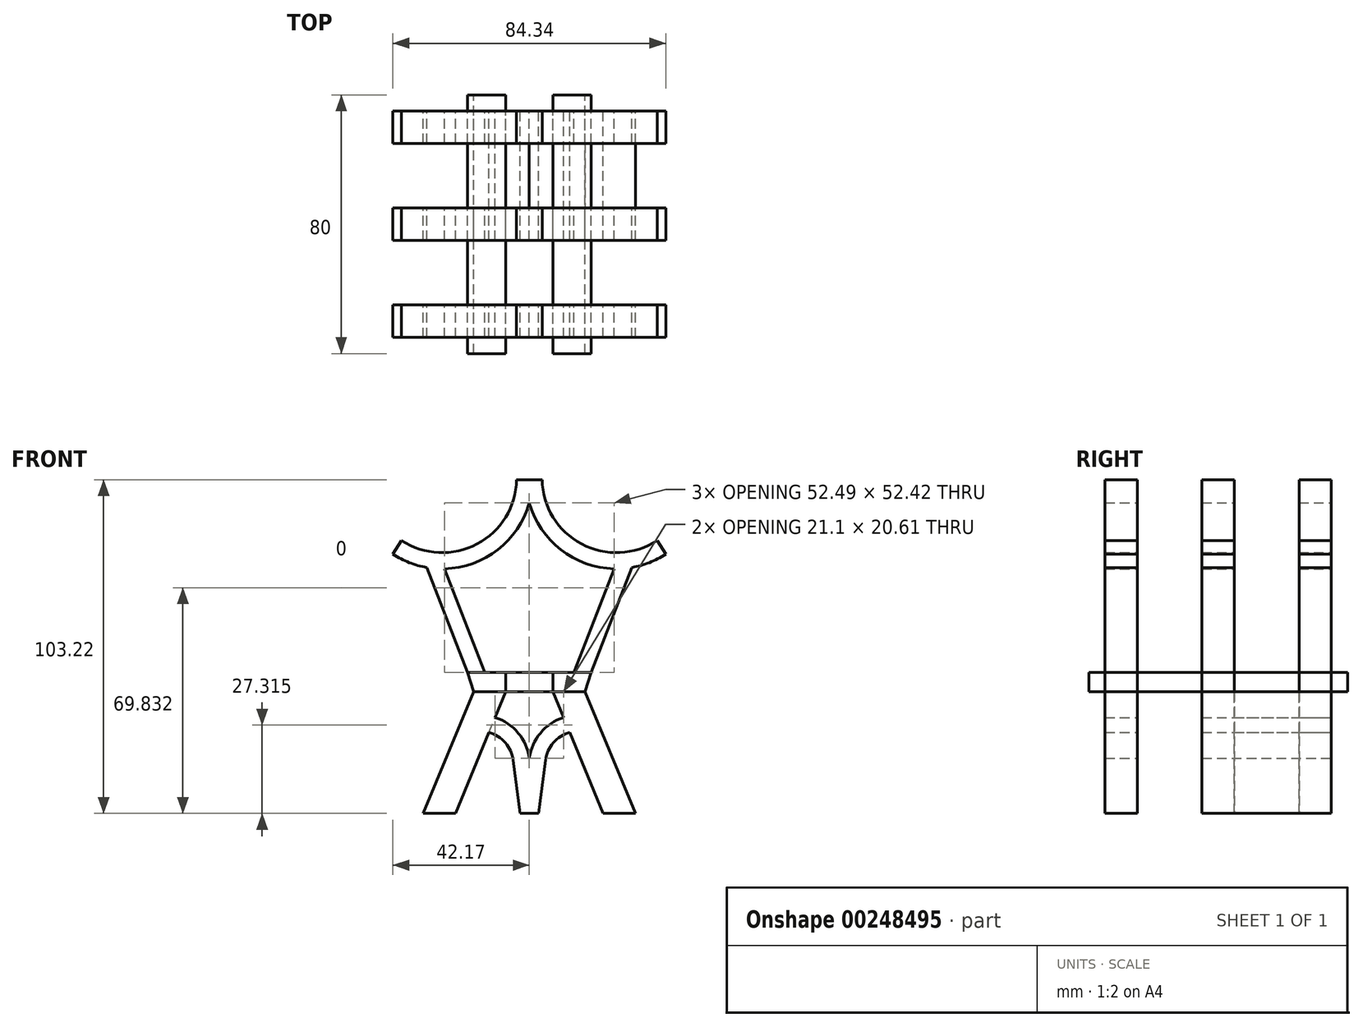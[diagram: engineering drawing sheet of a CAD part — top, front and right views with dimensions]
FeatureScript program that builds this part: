
annotation { "Feature Type Name" : "Feature", "Feature Type Description" : "" }
export const myFeature = defineFeature(function(context is Context, id is Id, definition is map)
    precondition{}
    {
        {
            var Q0;
            Q0=qCreatedBy(makeId("Front.planeOp"),FACE);
            var sketch = newSketch(context, id + "F0", { "sketchPlane" : qUnion([Q0])});
            skLineSegment(sketch, "E0", {"start": v(0, 0) * mm, "end": v(-19.13, 0) * mm});
            skLineSegment(sketch, "E1", {"start": v(-19.13, 0) * mm, "end": v(-31.73, 32.44) * mm});
            skArc(sketch, "E2", {"start": v(-42.17, 36.54) * mm, "mid": v(-17.07, 33.82) * mm, "end": v(0, 52.42) * mm});
            skArc(sketch, "E3.0", {"start": v(-39.52, 40.78) * mm, "mid": v(-16.18, 39.7) * mm, "end": v(-3.96, 59.6) * mm});
            skLineSegment(sketch, "E4", {"start": v(-42.17, 36.54) * mm, "end": v(-39.52, 40.78) * mm});
            skLineSegment(sketch, "E5", {"start": v(-3.96, 59.6) * mm, "end": v(1.04, 59.6) * mm});
            skLineSegment(sketch, "E6", {"start": v(-13.8, 0) * mm, "end": v(-26.24, 32.03) * mm});
            skLineSegment(sketch, "E7", {"start": v(0, -6) * mm, "end": v(-17.25, -6) * mm});
            skLineSegment(sketch, "E8.MirrorCS", {"start": v(42.17, 36.54) * mm, "end": v(39.52, 40.78) * mm});
            skLineSegment(sketch, "E9.MirrorCS", {"start": v(3.96, 59.6) * mm, "end": v(-1.04, 59.6) * mm});
            skLineSegment(sketch, "E10.MirrorCS", {"start": v(0, 0) * mm, "end": v(19.13, 0) * mm});
            skArc(sketch, "E11.MirrorCS", {"start": v(42.17, 36.54) * mm, "mid": v(17.07, 33.82) * mm, "end": v(0, 52.42) * mm});
            skArc(sketch, "E12.MirrorCS", {"start": v(39.52, 40.78) * mm, "mid": v(16.18, 39.7) * mm, "end": v(3.96, 59.6) * mm});
            skLineSegment(sketch, "E13.MirrorCS", {"start": v(19.13, 0) * mm, "end": v(31.73, 32.44) * mm});
            skLineSegment(sketch, "E14.MirrorCS", {"start": v(0, -6) * mm, "end": v(17.25, -6) * mm});
            skLineSegment(sketch, "E15.MirrorCS", {"start": v(13.8, 0) * mm, "end": v(26.24, 32.03) * mm});
            skLineSegment(sketch, "E16", {"start": v(-19.13, 0) * mm, "end": v(-17.25, -6) * mm});
            skLineSegment(sketch, "E17", {"start": v(17.25, -6) * mm, "end": v(19.13, 0) * mm});
            skLineSegment(sketch, "E18", {"start": v(-17.25, -6) * mm, "end": v(-32.84, -43.62) * mm});
            skLineSegment(sketch, "E19", {"start": v(-32.84, -43.62) * mm, "end": v(-22.84, -43.62) * mm});
            skLineSegment(sketch, "E20", {"start": v(-22.84, -43.62) * mm, "end": v(-7.25, -6) * mm});
            skLineSegment(sketch, "E21.MirrorCS", {"start": v(22.84, -43.62) * mm, "end": v(7.25, -6) * mm});
            skLineSegment(sketch, "E22.MirrorCS", {"start": v(17.25, -6) * mm, "end": v(32.84, -43.62) * mm});
            skLineSegment(sketch, "E23.MirrorCS", {"start": v(32.84, -43.62) * mm, "end": v(22.84, -43.62) * mm});
            skArc(sketch, "E24", {"start": v(0, -26.61) * mm, "mid": v(-3.43, -18.75) * mm, "end": v(-10.55, -13.96) * mm});
            skArc(sketch, "E25.0", {"start": v(-4.96, -27.25) * mm, "mid": v(-7.4, -21.79) * mm, "end": v(-12.48, -18.6) * mm});
            skLineSegment(sketch, "E26", {"start": v(-4.96, -27.25) * mm, "end": v(-2.86, -43.62) * mm});
            skArc(sketch, "E27.MirrorCS", {"start": v(0, -26.61) * mm, "mid": v(3.43, -18.75) * mm, "end": v(10.55, -13.96) * mm});
            skArc(sketch, "E28.MirrorCS", {"start": v(4.96, -27.25) * mm, "mid": v(7.4, -21.79) * mm, "end": v(12.48, -18.6) * mm});
            skLineSegment(sketch, "E29.MirrorCS", {"start": v(4.96, -27.25) * mm, "end": v(2.86, -43.62) * mm});
            skLineSegment(sketch, "E30", {"start": v(-2.86, -43.62) * mm, "end": v(2.86, -43.62) * mm});
            skPoint(sketch, "E31.orphan", {"position": v(-20.67, -14.25) * mm});
            skPoint(sketch, "E32.orphan", {"position": v(-18.88, -18.92) * mm});
            skPoint(sketch, "E33.orphan", {"position": v(20.67, -14.25) * mm});
            skPoint(sketch, "E34.orphan", {"position": v(18.88, -18.92) * mm});
            skSolve(sketch);
        }
        {
            var Q0;
            {var subQ0=sQuery(id+"F0.wireOp",EDGE,"E1");Q0=makeQuery(id+"F0.imprint","IMPRINT",FACE,{"disambiguationData":[TD([[makeQuery(id+"F0.imprint","IMPRINT",EDGE,{"derivedFrom":subQ0}),-1.0]])]});}
            var Q1;
            {var subQ3=sQuery(id+"F0.wireOp",EDGE,"E18");Q1=makeQuery(id+"F0.imprint","IMPRINT",FACE,{"disambiguationData":[TD([[makeQuery(id+"F0.imprint","IMPRINT",EDGE,{"derivedFrom":subQ3}),1.0]])]});}
            var Q2;
            {var subQ0=sQuery(id+"F0.wireOp",EDGE,"E13.MirrorCS");Q2=makeQuery(id+"F0.imprint","IMPRINT",FACE,{"disambiguationData":[TD([[makeQuery(id+"F0.imprint","IMPRINT",EDGE,{"derivedFrom":subQ0}),1.0]])]});}
            var Q3;
            {var subQ4=sQuery(id+"F0.wireOp",EDGE,"E22.MirrorCS");Q3=makeQuery(id+"F0.imprint","IMPRINT",FACE,{"disambiguationData":[TD([[makeQuery(id+"F0.imprint","IMPRINT",EDGE,{"derivedFrom":subQ4}),-1.0]])]});}
            var Q4;
            {var subQ1=sQuery(id+"F0.wireOp",EDGE,"E24");Q4=makeQuery(id+"F0.imprint","IMPRINT",FACE,{"disambiguationData":[TD([[makeQuery(id+"F0.imprint","IMPRINT",EDGE,{"derivedFrom":subQ1}),1.0]])]});}
            var Q5;
            {var subQ0=sQuery(id+"F0.wireOp",EDGE,"E16");Q5=makeQuery(id+"F0.imprint","IMPRINT",FACE,{"disambiguationData":[TD([[makeQuery(id+"F0.imprint","IMPRINT",EDGE,{"derivedFrom":subQ0}),1.0]])]});}
            var Q6;
            Q6=makeQuery(id+"F0.imprint","IMPRINT",FACE,{"disambiguationData":[TD([[makeQuery(id+"F0.imprint","IMPRINT",EDGE,{"derivedFrom":sQuery(id+"F0.wireOp",EDGE,"E3.0")}),-1.0]])]});
            extrude(context, id + "F1", {"entities" : qUnion([Q0, Q1, Q2, Q3, Q4, Q5, Q6]), "endBound" : BoundingType.SYMMETRIC, "depth" : 70 * mm});
        }
        {
            var Q0;
            Q0=qCreatedBy(makeId("Front.planeOp"),FACE);
            cPlane(context, id + "F2", {"entities" : qUnion([Q0]), "cplaneType" : CPlaneType.OFFSET, "offset" : 5 * mm, "width" : 150 * mm, "height" : 150 * mm});
        }
        {
            var Q0;
            Q0=qCreatedBy(makeId("Front.planeOp"),FACE);
            cPlane(context, id + "F3", {"entities" : qUnion([Q0]), "cplaneType" : CPlaneType.OFFSET, "offset" : 5 * mm, "oppositeDirection" : true, "width" : 150 * mm, "height" : 150 * mm});
        }
        {
            var Q0;
            Q0=qCreatedBy(id+"F2.planeOp",FACE);
            var sketch = newSketch(context, id + "F4", { "sketchPlane" : qUnion([Q0])});
            skLineSegment(sketch, "E35.0", {"start": v(-4.96, -27.25) * mm, "end": v(-2.86, -43.62) * mm});
            skLineSegment(sketch, "E35.1", {"start": v(-32.84, -43.62) * mm, "end": v(-22.84, -43.62) * mm});
            skLineSegment(sketch, "E35.2", {"start": v(19.13, 0) * mm, "end": v(31.73, 32.44) * mm});
            skLineSegment(sketch, "E35.3", {"start": v(0, -6) * mm, "end": v(17.25, -6) * mm});
            skLineSegment(sketch, "E35.4", {"start": v(13.8, 0) * mm, "end": v(26.24, 32.03) * mm});
            skLineSegment(sketch, "E35.5", {"start": v(0, 0) * mm, "end": v(-19.13, 0) * mm});
            skLineSegment(sketch, "E35.6", {"start": v(-19.13, 0) * mm, "end": v(-31.73, 32.44) * mm});
            skArc(sketch, "E35.7", {"start": v(-42.17, 36.54) * mm, "mid": v(-17.07, 33.82) * mm, "end": v(0, 52.42) * mm});
            skArc(sketch, "E35.8", {"start": v(-39.52, 40.78) * mm, "mid": v(-16.18, 39.7) * mm, "end": v(-3.96, 59.6) * mm});
            skLineSegment(sketch, "E35.9", {"start": v(-42.17, 36.54) * mm, "end": v(-39.52, 40.78) * mm});
            skLineSegment(sketch, "E35.10", {"start": v(-13.8, 0) * mm, "end": v(-26.24, 32.03) * mm});
            skLineSegment(sketch, "E35.11", {"start": v(0, -6) * mm, "end": v(-17.25, -6) * mm});
            skLineSegment(sketch, "E35.12", {"start": v(0, 0) * mm, "end": v(19.13, 0) * mm});
            skArc(sketch, "E35.13", {"start": v(42.17, 36.54) * mm, "mid": v(17.07, 33.82) * mm, "end": v(0, 52.42) * mm});
            skArc(sketch, "E35.14", {"start": v(39.52, 40.78) * mm, "mid": v(16.18, 39.7) * mm, "end": v(3.96, 59.6) * mm});
            skArc(sketch, "E35.15", {"start": v(0, -26.61) * mm, "mid": v(3.43, -18.75) * mm, "end": v(10.55, -13.96) * mm});
            skLineSegment(sketch, "E35.16", {"start": v(32.84, -43.62) * mm, "end": v(22.84, -43.62) * mm});
            skLineSegment(sketch, "E35.17", {"start": v(-22.84, -43.62) * mm, "end": v(-7.25, -6) * mm});
            skLineSegment(sketch, "E35.18", {"start": v(4.96, -27.25) * mm, "end": v(2.86, -43.62) * mm});
            skLineSegment(sketch, "E35.19", {"start": v(-19.13, 0) * mm, "end": v(-17.25, -6) * mm});
            skArc(sketch, "E35.20", {"start": v(4.96, -27.25) * mm, "mid": v(7.4, -21.79) * mm, "end": v(12.48, -18.6) * mm});
            skArc(sketch, "E35.21", {"start": v(0, -26.61) * mm, "mid": v(-3.43, -18.75) * mm, "end": v(-10.55, -13.96) * mm});
            skLineSegment(sketch, "E35.22", {"start": v(22.84, -43.62) * mm, "end": v(7.25, -6) * mm});
            skLineSegment(sketch, "E35.23", {"start": v(-2.86, -43.62) * mm, "end": v(2.86, -43.62) * mm});
            skLineSegment(sketch, "E35.24", {"start": v(17.25, -6) * mm, "end": v(19.13, 0) * mm});
            skArc(sketch, "E35.25", {"start": v(-4.96, -27.25) * mm, "mid": v(-7.4, -21.79) * mm, "end": v(-12.48, -18.6) * mm});
            skLineSegment(sketch, "E35.26", {"start": v(17.25, -6) * mm, "end": v(32.84, -43.62) * mm});
            skLineSegment(sketch, "E35.27", {"start": v(-17.25, -6) * mm, "end": v(-32.84, -43.62) * mm});
            skLineSegment(sketch, "E35.28", {"start": v(-3.96, 59.6) * mm, "end": v(1.04, 59.6) * mm});
            skLineSegment(sketch, "E35.29", {"start": v(3.96, 59.6) * mm, "end": v(-1.04, 59.6) * mm});
            skLineSegment(sketch, "E35.30", {"start": v(42.17, 36.54) * mm, "end": v(39.52, 40.78) * mm});
            skSolve(sketch);
        }
        {
            var Q0;
            Q0=qCreatedBy(id+"F3.planeOp",FACE);
            var sketch = newSketch(context, id + "F5", { "sketchPlane" : qUnion([Q0])});
            skArc(sketch, "E36.0.0", {"start": v(26.24, 32.03) * mm, "mid": v(29, 32.1) * mm, "end": v(31.73, 32.44) * mm});
            skArc(sketch, "E36.0.1", {"start": v(31.73, 32.44) * mm, "mid": v(37.16, 33.96) * mm, "end": v(42.17, 36.54) * mm});
            skLineSegment(sketch, "E36.0.2", {"start": v(42.17, 36.54) * mm, "end": v(39.52, 40.78) * mm});
            skArc(sketch, "E36.0.3", {"start": v(39.52, 40.78) * mm, "mid": v(16.18, 39.7) * mm, "end": v(3.96, 59.6) * mm});
            skLineSegment(sketch, "E36.0.4", {"start": v(3.96, 59.6) * mm, "end": v(-1.04, 59.6) * mm});
            skLineSegment(sketch, "E36.0.5", {"start": v(-1.04, 59.6) * mm, "end": v(-3.96, 59.6) * mm});
            skArc(sketch, "E36.0.6", {"start": v(-3.96, 59.6) * mm, "mid": v(-16.18, 39.7) * mm, "end": v(-39.52, 40.78) * mm});
            skLineSegment(sketch, "E36.0.7", {"start": v(-39.52, 40.78) * mm, "end": v(-42.17, 36.54) * mm});
            skArc(sketch, "E36.0.8", {"start": v(-42.17, 36.54) * mm, "mid": v(-37.16, 33.96) * mm, "end": v(-31.73, 32.44) * mm});
            skArc(sketch, "E36.0.9", {"start": v(-31.73, 32.44) * mm, "mid": v(-29, 32.1) * mm, "end": v(-26.24, 32.03) * mm});
            skArc(sketch, "E36.0.10", {"start": v(-26.24, 32.03) * mm, "mid": v(-9.77, 37.9) * mm, "end": v(0, 52.42) * mm});
            skArc(sketch, "E36.0.11", {"start": v(0, 52.42) * mm, "mid": v(9.77, 37.9) * mm, "end": v(26.24, 32.03) * mm});
            skLineSegment(sketch, "E37.0.0", {"start": v(-19.13, 0) * mm, "end": v(-13.8, 0) * mm});
            skLineSegment(sketch, "E37.0.1", {"start": v(-13.8, 0) * mm, "end": v(-26.24, 32.03) * mm});
            skArc(sketch, "E37.0.2", {"start": v(-26.24, 32.03) * mm, "mid": v(-29, 32.1) * mm, "end": v(-31.73, 32.44) * mm});
            skLineSegment(sketch, "E37.0.3", {"start": v(-31.73, 32.44) * mm, "end": v(-19.13, 0) * mm});
            skLineSegment(sketch, "E38.0.0", {"start": v(19.13, 0) * mm, "end": v(13.8, 0) * mm});
            skLineSegment(sketch, "E38.0.1", {"start": v(13.8, 0) * mm, "end": v(0, 0) * mm});
            skLineSegment(sketch, "E38.0.2", {"start": v(0, 0) * mm, "end": v(-13.8, 0) * mm});
            skLineSegment(sketch, "E38.0.3", {"start": v(-13.8, 0) * mm, "end": v(-19.13, 0) * mm});
            skLineSegment(sketch, "E38.0.4", {"start": v(-19.13, 0) * mm, "end": v(-17.25, -6) * mm});
            skLineSegment(sketch, "E38.0.5", {"start": v(-17.25, -6) * mm, "end": v(-7.25, -6) * mm});
            skLineSegment(sketch, "E38.0.6", {"start": v(-7.25, -6) * mm, "end": v(0, -6) * mm});
            skLineSegment(sketch, "E38.0.7", {"start": v(0, -6) * mm, "end": v(7.25, -6) * mm});
            skLineSegment(sketch, "E38.0.8", {"start": v(7.25, -6) * mm, "end": v(17.25, -6) * mm});
            skLineSegment(sketch, "E38.0.9", {"start": v(17.25, -6) * mm, "end": v(19.13, 0) * mm});
            skLineSegment(sketch, "E39.0.0", {"start": v(19.13, 0) * mm, "end": v(31.73, 32.44) * mm});
            skArc(sketch, "E39.0.1", {"start": v(31.73, 32.44) * mm, "mid": v(29, 32.1) * mm, "end": v(26.24, 32.03) * mm});
            skLineSegment(sketch, "E39.0.2", {"start": v(26.24, 32.03) * mm, "end": v(13.8, 0) * mm});
            skLineSegment(sketch, "E39.0.3", {"start": v(13.8, 0) * mm, "end": v(19.13, 0) * mm});
            skLineSegment(sketch, "E40.0.0", {"start": v(-12.48, -18.6) * mm, "end": v(-10.55, -13.96) * mm});
            skLineSegment(sketch, "E40.0.1", {"start": v(-10.55, -13.96) * mm, "end": v(-7.25, -6) * mm});
            skLineSegment(sketch, "E40.0.2", {"start": v(-7.25, -6) * mm, "end": v(-17.25, -6) * mm});
            skLineSegment(sketch, "E40.0.3", {"start": v(-17.25, -6) * mm, "end": v(-32.84, -43.62) * mm});
            skLineSegment(sketch, "E40.0.4", {"start": v(-32.84, -43.62) * mm, "end": v(-22.84, -43.62) * mm});
            skLineSegment(sketch, "E40.0.5", {"start": v(-22.84, -43.62) * mm, "end": v(-12.48, -18.6) * mm});
            skArc(sketch, "E41.0.0", {"start": v(4.96, -27.25) * mm, "mid": v(7.4, -21.79) * mm, "end": v(12.48, -18.6) * mm});
            skLineSegment(sketch, "E41.0.1", {"start": v(12.48, -18.6) * mm, "end": v(10.55, -13.96) * mm});
            skArc(sketch, "E41.0.2", {"start": v(10.55, -13.96) * mm, "mid": v(3.43, -18.75) * mm, "end": v(0, -26.61) * mm});
            skArc(sketch, "E41.0.3", {"start": v(0, -26.61) * mm, "mid": v(-3.43, -18.75) * mm, "end": v(-10.55, -13.96) * mm});
            skLineSegment(sketch, "E41.0.4", {"start": v(-10.55, -13.96) * mm, "end": v(-12.48, -18.6) * mm});
            skArc(sketch, "E41.0.5", {"start": v(-12.48, -18.6) * mm, "mid": v(-7.4, -21.79) * mm, "end": v(-4.96, -27.25) * mm});
            skLineSegment(sketch, "E41.0.6", {"start": v(-4.96, -27.25) * mm, "end": v(-2.86, -43.62) * mm});
            skLineSegment(sketch, "E41.0.7", {"start": v(-2.86, -43.62) * mm, "end": v(2.86, -43.62) * mm});
            skLineSegment(sketch, "E41.0.8", {"start": v(2.86, -43.62) * mm, "end": v(4.96, -27.25) * mm});
            skLineSegment(sketch, "E42.0.0", {"start": v(10.55, -13.96) * mm, "end": v(12.48, -18.6) * mm});
            skLineSegment(sketch, "E42.0.1", {"start": v(12.48, -18.6) * mm, "end": v(22.84, -43.62) * mm});
            skLineSegment(sketch, "E42.0.2", {"start": v(22.84, -43.62) * mm, "end": v(32.84, -43.62) * mm});
            skLineSegment(sketch, "E42.0.3", {"start": v(32.84, -43.62) * mm, "end": v(17.25, -6) * mm});
            skLineSegment(sketch, "E42.0.4", {"start": v(17.25, -6) * mm, "end": v(7.25, -6) * mm});
            skLineSegment(sketch, "E42.0.5", {"start": v(7.25, -6) * mm, "end": v(10.55, -13.96) * mm});
            skSolve(sketch);
        }
        {
            var Q0;
            Q0=makeQuery(id+"F4.imprint","IMPRINT",FACE,{"disambiguationData":[TD([[makeQuery(id+"F4.imprint","IMPRINT",EDGE,{"derivedFrom":sQuery(id+"F4.wireOp",EDGE,"E35.8")}),-1.0]])]});
            var Q1;
            {var subQ0=sQuery(id+"F4.wireOp",EDGE,"E35.2");Q1=makeQuery(id+"F4.imprint","IMPRINT",FACE,{"disambiguationData":[TD([[makeQuery(id+"F4.imprint","IMPRINT",EDGE,{"derivedFrom":subQ0}),1.0]])]});}
            var Q2;
            {var subQ7=sQuery(id+"F4.wireOp",EDGE,"E35.19");Q2=makeQuery(id+"F4.imprint","IMPRINT",FACE,{"disambiguationData":[TD([[makeQuery(id+"F4.imprint","IMPRINT",EDGE,{"derivedFrom":subQ7}),1.0]])]});}
            var Q3;
            {var subQ0=sQuery(id+"F4.wireOp",EDGE,"E35.6");Q3=makeQuery(id+"F4.imprint","IMPRINT",FACE,{"disambiguationData":[TD([[makeQuery(id+"F4.imprint","IMPRINT",EDGE,{"derivedFrom":subQ0}),-1.0]])]});}
            var Q4;
            {var subQ3=sQuery(id+"F4.wireOp",EDGE,"E35.1");Q4=makeQuery(id+"F4.imprint","IMPRINT",FACE,{"disambiguationData":[TD([[makeQuery(id+"F4.imprint","IMPRINT",EDGE,{"derivedFrom":subQ3}),1.0]])]});}
            var Q5;
            Q5=makeQuery(id+"F4.imprint","IMPRINT",FACE,{"disambiguationData":[TD([[makeQuery(id+"F4.imprint","IMPRINT",EDGE,{"derivedFrom":sQuery(id+"F4.wireOp",EDGE,"E35.0")}),1.0]])]});
            var Q6;
            {var subQ3=sQuery(id+"F4.wireOp",EDGE,"E35.16");Q6=makeQuery(id+"F4.imprint","IMPRINT",FACE,{"disambiguationData":[TD([[makeQuery(id+"F4.imprint","IMPRINT",EDGE,{"derivedFrom":subQ3}),-1.0]])]});}
            extrude(context, id + "F6", {"entities" : qUnion([Q0, Q1, Q2, Q3, Q4, Q5, Q6]), "operationType" : NewBodyOperationType.REMOVE, "depth" : 20 * mm});
        }
        {
            var Q0;
            Q0=makeQuery(id+"F5.imprint","IMPRINT",FACE,{"disambiguationData":[TD([[makeQuery(id+"F5.imprint","IMPRINT",EDGE,{"derivedFrom":sQuery(id+"F5.wireOp",EDGE,"E36.0.1")}),1.0]])]});
            var Q1;
            Q1=makeQuery(id+"F5.imprint","IMPRINT",FACE,{"disambiguationData":[TD([[makeQuery(id+"F5.imprint","IMPRINT",EDGE,{"derivedFrom":sQuery(id+"F5.wireOp",EDGE,"E37.0.1")}),1.0]])]});
            var Q2;
            Q2=makeQuery(id+"F5.imprint","IMPRINT",FACE,{"disambiguationData":[TD([[makeQuery(id+"F5.imprint","IMPRINT",EDGE,{"derivedFrom":sQuery(id+"F5.wireOp",EDGE,"E38.0.1")}),1.0]])]});
            var Q3;
            Q3=makeQuery(id+"F5.imprint","IMPRINT",FACE,{"disambiguationData":[TD([[makeQuery(id+"F5.imprint","IMPRINT",EDGE,{"derivedFrom":sQuery(id+"F5.wireOp",EDGE,"E42.0.0")}),1.0]])]});
            var Q4;
            Q4=makeQuery(id+"F5.imprint","IMPRINT",FACE,{"disambiguationData":[TD([[makeQuery(id+"F5.imprint","IMPRINT",EDGE,{"derivedFrom":sQuery(id+"F5.wireOp",EDGE,"E41.0.0")}),1.0]])]});
            var Q5;
            Q5=makeQuery(id+"F5.imprint","IMPRINT",FACE,{"disambiguationData":[TD([[makeQuery(id+"F5.imprint","IMPRINT",EDGE,{"derivedFrom":sQuery(id+"F5.wireOp",EDGE,"E40.0.1")}),1.0]])]});
            var Q6;
            Q6=makeQuery(id+"F5.imprint","IMPRINT",FACE,{"disambiguationData":[TD([[makeQuery(id+"F5.imprint","IMPRINT",EDGE,{"derivedFrom":sQuery(id+"F5.wireOp",EDGE,"E39.0.0")}),1.0]])]});
            extrude(context, id + "F7", {"entities" : qUnion([Q0, Q1, Q2, Q3, Q4, Q5, Q6]), "operationType" : NewBodyOperationType.REMOVE, "oppositeDirection" : true, "depth" : 20 * mm});
        }
        {
            var Q0;
            Q0=qCreatedBy(makeId("Front.planeOp"),FACE);
            var sketch = newSketch(context, id + "F8", { "sketchPlane" : qUnion([Q0])});
            skLineSegment(sketch, "E43.0.0", {"start": v(19.13, 0) * mm, "end": v(13.8, 0) * mm});
            skLineSegment(sketch, "E43.0.1", {"start": v(13.8, 0) * mm, "end": v(0, 0) * mm});
            skLineSegment(sketch, "E43.0.2", {"start": v(0, 0) * mm, "end": v(-13.8, 0) * mm});
            skLineSegment(sketch, "E43.0.3", {"start": v(-13.8, 0) * mm, "end": v(-19.13, 0) * mm});
            skLineSegment(sketch, "E43.0.4", {"start": v(-19.13, 0) * mm, "end": v(-17.25, -6) * mm});
            skLineSegment(sketch, "E43.0.5", {"start": v(-17.25, -6) * mm, "end": v(-7.25, -6) * mm});
            skLineSegment(sketch, "E43.0.6", {"start": v(-7.25, -6) * mm, "end": v(0, -6) * mm});
            skLineSegment(sketch, "E43.0.7", {"start": v(0, -6) * mm, "end": v(7.25, -6) * mm});
            skLineSegment(sketch, "E43.0.8", {"start": v(7.25, -6) * mm, "end": v(17.25, -6) * mm});
            skLineSegment(sketch, "E43.0.9", {"start": v(17.25, -6) * mm, "end": v(19.13, 0) * mm});
            skLineSegment(sketch, "E44", {"start": v(-7.25, 0) * mm, "end": v(-7.25, -6) * mm});
            skLineSegment(sketch, "E45.MirrorCS", {"start": v(7.25, 0) * mm, "end": v(7.25, -6) * mm});
            skLineSegment(sketch, "E46", {"start": v(-13.8, 0) * mm, "end": v(-7.25, 0) * mm});
            skLineSegment(sketch, "E47", {"start": v(7.25, 0) * mm, "end": v(13.8, 0) * mm});
            skSolve(sketch);
        }
        {
            var Q0;
            Q0=makeQuery(id+"F8.imprint","IMPRINT",FACE,{"disambiguationData":[TD([[makeQuery(id+"F8.imprint","IMPRINT",EDGE,{"derivedFrom":sQuery(id+"F8.wireOp",EDGE,"E43.0.3")}),1.0]])]});
            var Q1;
            Q1=makeQuery(id+"F8.imprint","IMPRINT",FACE,{"disambiguationData":[TD([[makeQuery(id+"F8.imprint","IMPRINT",EDGE,{"derivedFrom":sQuery(id+"F8.wireOp",EDGE,"E43.0.0")}),1.0]])]});
            extrude(context, id + "F9", {"entities" : qUnion([Q0, Q1]), "endBound" : BoundingType.SYMMETRIC, "depth" : 80 * mm});
        }
    });
